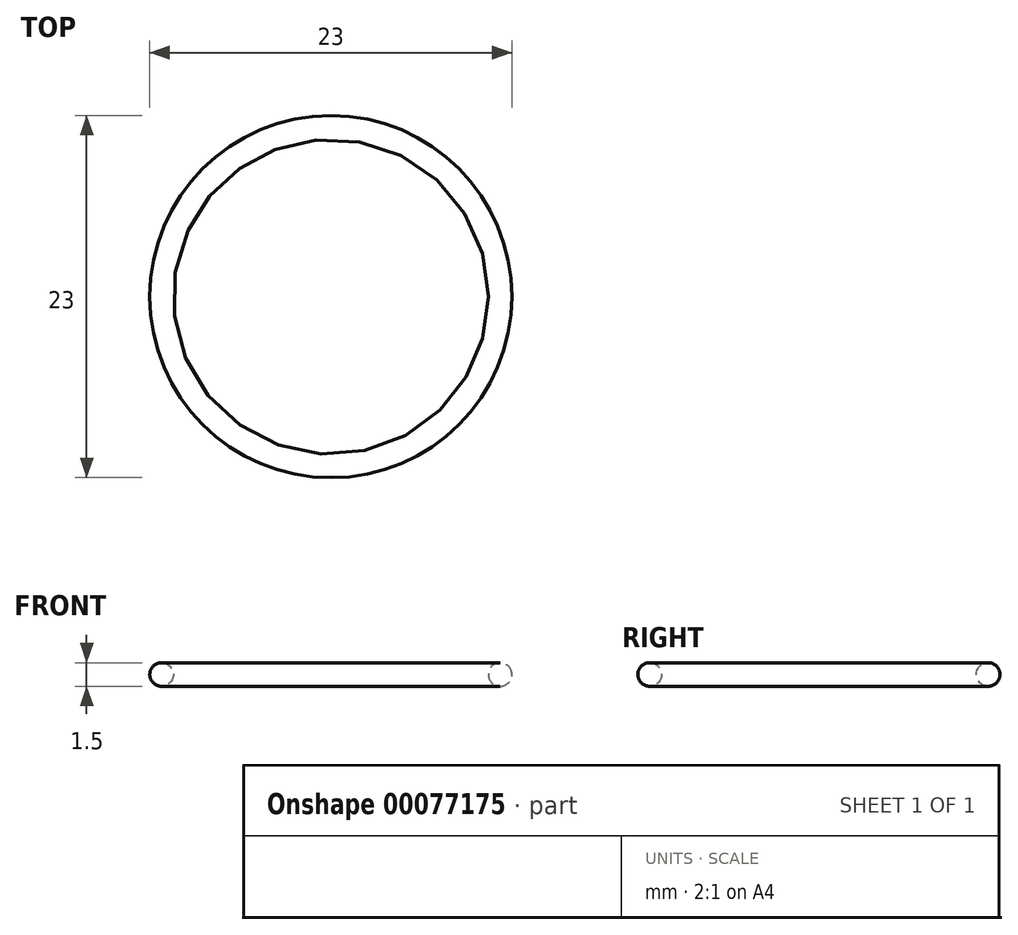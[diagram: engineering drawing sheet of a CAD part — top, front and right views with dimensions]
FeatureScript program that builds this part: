
annotation { "Feature Type Name" : "Feature", "Feature Type Description" : "" }
export const myFeature = defineFeature(function(context is Context, id is Id, definition is map)
    precondition{}
    {
        {
            var Q0;
            Q0=qCreatedBy(makeId("Top.planeOp"),FACE);
            var sketch = newSketch(context, id + "F0", { "sketchPlane" : qUnion([Q0])});
            skCircle(sketch, "E0", {"center": v(0, 0) * mm, "radius": 10 * mm});
            skCircle(sketch, "E1", {"center": v(0, 0) * mm, "radius": 11.5 * mm});
            skSolve(sketch);
        }
        {
            var Q0;
            Q0=qSketchRegion(id+"F0",true);
            extrude(context, id + "F1", {"entities" : qUnion([Q0]), "depth" : 1.5 * mm});
        }
        {
            var Q0;
            Q0=makeQuery(id+"F1.opExtrude","CAP_EDGE",EDGE,{"disambiguationData":[OSD([sQuery(id+"F0.wireOp",EDGE,"E0")])],"isStart":false});
            var Q1;
            Q1=makeQuery(id+"F1.opExtrude","CAP_EDGE",EDGE,{"disambiguationData":[OSD([sQuery(id+"F0.wireOp",EDGE,"E1")])],"isStart":false});
            var Q2;
            Q2=makeQuery(id+"F1.opExtrude","CAP_EDGE",EDGE,{"disambiguationData":[OSD([sQuery(id+"F0.wireOp",EDGE,"E1")])],"isStart":true});
            var Q3;
            Q3=makeQuery(id+"F1.opExtrude","CAP_EDGE",EDGE,{"disambiguationData":[OSD([sQuery(id+"F0.wireOp",EDGE,"E0")])],"isStart":true});
            fillet(context, id + "F2", {"entities" : qUnion([Q0, Q1, Q2, Q3]), "radius" : .75 * mm, "tangentPropagation" : true, "allowEdgeOverflow" : false});
        }
    });
